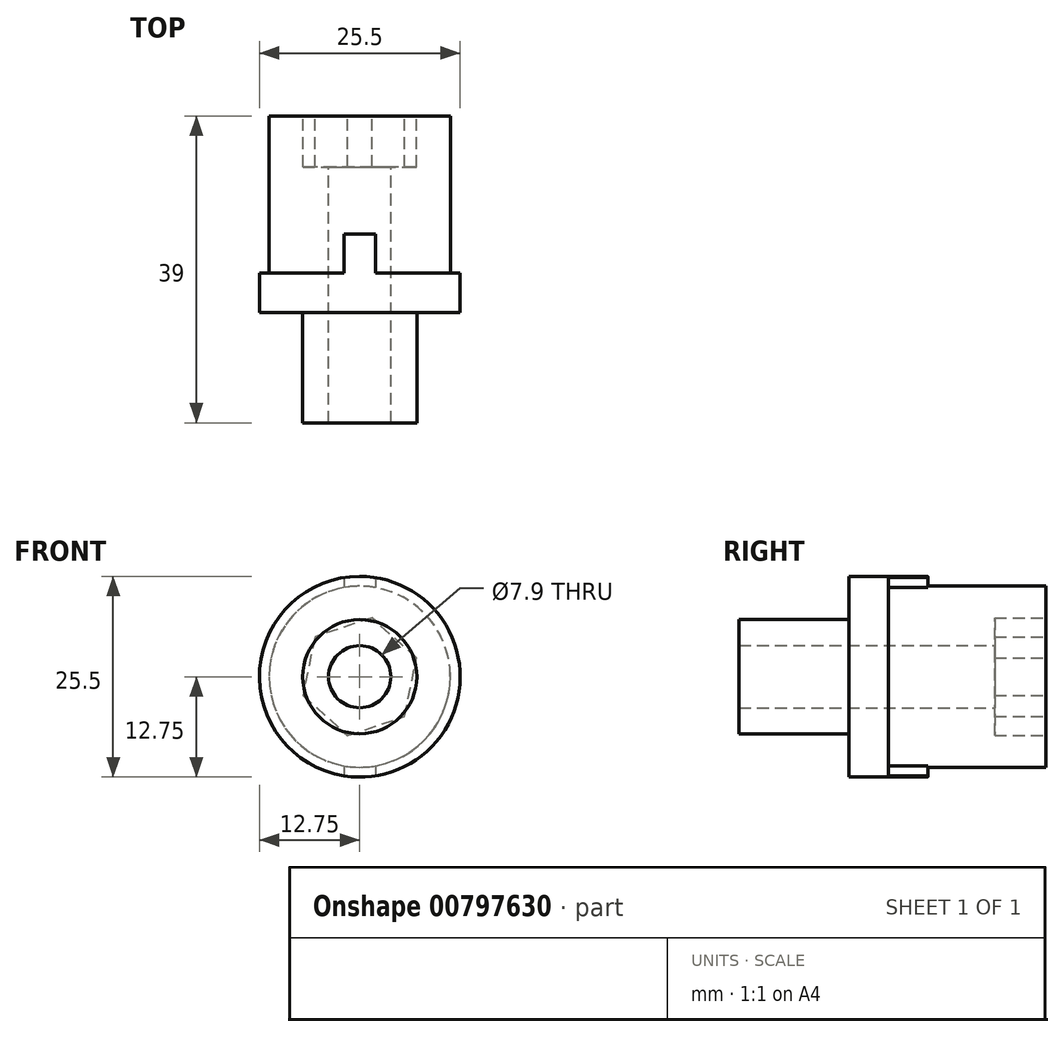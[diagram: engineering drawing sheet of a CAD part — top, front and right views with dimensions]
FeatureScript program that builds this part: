
annotation { "Feature Type Name" : "Feature", "Feature Type Description" : "" }
export const myFeature = defineFeature(function(context is Context, id is Id, definition is map)
    precondition{}
    {
        {
            var Q0;
            Q0=qCreatedBy(makeId("Front.planeOp"),FACE);
            var sketch = newSketch(context, id + "F0", { "sketchPlane" : qUnion([Q0])});
            skCircle(sketch, "E0", {"center": v(0, 0) * mm, "radius": 7.25 * mm});
            skSolve(sketch);
        }
        {
            var Q0;
            Q0=makeQuery(id+"F0.imprint","IMPRINT",FACE,{"disambiguationData":[TD([[makeQuery(id+"F0.imprint","IMPRINT",EDGE,{"derivedFrom":sQuery(id+"F0.wireOp",EDGE,"E0")}),1.0]])]});
            extrude(context, id + "F1", {"entities" : qUnion([Q0]), "depth" : 14 * mm, "offsetDistance" : 25 * mm});
        }
        {
            var Q0;
            Q0=makeQuery(id+"F1.opExtrude","CAP_FACE",FACE,{"disambiguationData":[OSD([sQuery(id+"F0.wireOp",EDGE,"E0")])],"isStart":true});
            var sketch = newSketch(context, id + "F2", { "sketchPlane" : qUnion([Q0])});
            skCircle(sketch, "E1", {"center": v(0, 0) * mm, "radius": 9.25 * mm});
            skCircle(sketch, "E2", {"center": v(0, 0) * mm, "radius": 11.25 * mm});
            skSolve(sketch);
        }
        {
            var Q0;
            Q0=makeQuery(id+"F1.opExtrude","CAP_FACE",FACE,{"disambiguationData":[OSD([sQuery(id+"F0.wireOp",EDGE,"E0")])],"isStart":false});
            var sketch = newSketch(context, id + "F3", { "sketchPlane" : qUnion([Q0])});
            skCircle(sketch, "E3", {"center": v(0, 0) * mm, "radius": 3 * mm});
            skSolve(sketch);
        }
        {
            var Q0;
            Q0=makeQuery(id+"F3.imprint","IMPRINT",FACE,{"disambiguationData":[TD([[makeQuery(id+"F3.imprint","IMPRINT",EDGE,{"derivedFrom":sQuery(id+"F3.wireOp",EDGE,"E3")}),1.0]])]});
            extrude(context, id + "F4", {"entities" : qUnion([Q0]), "operationType" : NewBodyOperationType.REMOVE, "endBound" : BoundingType.THROUGH_ALL, "oppositeDirection" : true, "depth" : 25 * mm, "offsetDistance" : 25 * mm});
        }
        {
            var Q0;
            Q0=makeQuery(id+"F2.imprint","IMPRINT",FACE,{"disambiguationData":[TD([[makeQuery(id+"F2.imprint","IMPRINT",EDGE,{"derivedFrom":sQuery(id+"F2.wireOp",EDGE,"E1")}),1.0]])]});
            cPlane(context, id + "F5", {"entities" : qUnion([Q0]), "cplaneType" : CPlaneType.OFFSET, "offset" : 0 * mm, "width" : 150 * mm, "height" : 150 * mm});
        }
        {
            var Q0;
            Q0=qCreatedBy(id+"F5.planeOp",FACE);
            var sketch = newSketch(context, id + "F6", { "sketchPlane" : qUnion([Q0])});
            skCircle(sketch, "E4", {"center": v(0, 0) * mm, "radius": 12.75 * mm});
            skSolve(sketch);
        }
        {
            var Q0;
            Q0=qSketchRegion(id+"F6",true);
            extrude(context, id + "F7", {"entities" : qUnion([Q0]), "operationType" : NewBodyOperationType.ADD, "depth" : 25 * mm, "offsetDistance" : 25 * mm});
        }
        {
            var Q0;
            Q0=makeQuery(id+"F7.opExtrude","CAP_FACE",FACE,{"disambiguationData":[OSD([sQuery(id+"F6.wireOp",EDGE,"E4")])],"isStart":false});
            var sketch = newSketch(context, id + "F8", { "sketchPlane" : qUnion([Q0])});
            skCircle(sketch, "E5", {"center": v(0, 0) * mm, "radius": 3.95 * mm});
            skSolve(sketch);
        }
        {
            var Q0;
            Q0=makeQuery(id+"F8.imprint","IMPRINT",FACE,{"disambiguationData":[TD([[makeQuery(id+"F8.imprint","IMPRINT",EDGE,{"derivedFrom":sQuery(id+"F8.wireOp",EDGE,"E5")}),1.0]])]});
            extrude(context, id + "F9", {"entities" : qUnion([Q0]), "operationType" : NewBodyOperationType.REMOVE, "endBound" : BoundingType.THROUGH_ALL, "oppositeDirection" : true, "depth" : 25 * mm, "offsetDistance" : 25 * mm});
        }
        {
            var Q0;
            Q0=makeQuery(id+"F7.opExtrude","CAP_FACE",FACE,{"disambiguationData":[OSD([sQuery(id+"F6.wireOp",EDGE,"E4")])],"isStart":false});
            var sketch = newSketch(context, id + "F10", { "sketchPlane" : qUnion([Q0])});
            skCircle(sketch, "E6", {"center": v(0, 0) * mm, "radius": 11.5 * mm});
            skSolve(sketch);
        }
        {
            var Q0;
            Q0=makeQuery(id+"F10.imprint","IMPRINT",FACE,{"disambiguationData":[TD([[makeQuery(id+"F10.imprint","IMPRINT",EDGE,{"derivedFrom":sQuery(id+"F10.wireOp",EDGE,"E6")}),-1.0]])]});
            extrude(context, id + "F11", {"entities" : qUnion([Q0]), "operationType" : NewBodyOperationType.REMOVE, "oppositeDirection" : true, "depth" : 20 * mm, "offsetDistance" : 25 * mm});
        }
        {
            var Q0;
            Q0=makeQuery(id+"F11.boolean.opBoolean","COPY",FACE,{"derivedFrom":makeQuery(id+"F11.opExtrude","CAP_FACE",FACE,{"disambiguationData":[OSD([sQuery(id+"F6.wireOp",EDGE,"E4"),sQuery(id+"F10.wireOp",EDGE,"E6")])],"isStart":false})});
            var sketch = newSketch(context, id + "F12", { "sketchPlane" : qUnion([Q0])});
            skLineSegment(sketch, "E7", {"start": v(0, 13.66) * mm, "end": v(0, -14.8) * mm, "construction": true});
            skLineSegment(sketch, "E8", {"start": v(-2, 12.6) * mm, "end": v(-2, 11.32) * mm});
            skLineSegment(sketch, "E9", {"start": v(2, 12.6) * mm, "end": v(2, 11.32) * mm});
            skLineSegment(sketch, "E10", {"start": v(-14.5, 0) * mm, "end": v(13.95, 0) * mm, "construction": true});
            skLineSegment(sketch, "E11.MirrorCS", {"start": v(-6, 12.6) * mm, "end": v(-6, 11.32) * mm});
            skLineSegment(sketch, "E12.MirrorCS", {"start": v(10.5, 0) * mm, "end": v(-17.95, 0) * mm, "construction": true});
            skLineSegment(sketch, "E13", {"start": v(-2, -11.32) * mm, "end": v(-2, -12.6) * mm});
            skLineSegment(sketch, "E14", {"start": v(2, -11.32) * mm, "end": v(2, -12.6) * mm});
            skPoint(sketch, "E15.MirrorCS.end.orphan", {"position": v(-6, 11.32) * mm});
            skPoint(sketch, "E15.MirrorCS.start.orphan", {"position": v(-6, 12.6) * mm});
            skSolve(sketch);
        }
        {
            var Q0;
            {var subQ0=sQuery(id+"F12.wireOp",EDGE,"E8");Q0=makeQuery(id+"F12.imprint","IMPRINT",FACE,{"disambiguationData":[TD([[makeQuery(id+"F12.imprint","IMPRINT",EDGE,{"derivedFrom":subQ0}),1.0]])]});}
            var Q1;
            {var subQ0=sQuery(id+"F12.wireOp",EDGE,"E13");Q1=makeQuery(id+"F12.imprint","IMPRINT",FACE,{"disambiguationData":[TD([[makeQuery(id+"F12.imprint","IMPRINT",EDGE,{"derivedFrom":subQ0}),1.0]])]});}
            extrude(context, id + "F13", {"entities" : qUnion([Q0, Q1]), "operationType" : NewBodyOperationType.ADD, "depth" : 5 * mm, "offsetDistance" : 25 * mm});
        }
        {
            var Q0;
            Q0=makeQuery(id+"F7.opExtrude","CAP_FACE",FACE,{"disambiguationData":[OSD([sQuery(id+"F6.wireOp",EDGE,"E4")])],"isStart":false});
            var sketch = newSketch(context, id + "F14", { "sketchPlane" : qUnion([Q0])});
            skCircle(sketch, "E16.cCircle", {"center": v(0, 0) * mm, "radius": 6.6 * mm, "construction": true});
            skLineSegment(sketch, "E16.0", {"start": v(-1.53, 7.46) * mm, "end": v(5.7, 5.06) * mm});
            skLineSegment(sketch, "E16.1", {"start": v(5.7, 5.06) * mm, "end": v(7.23, -2.4) * mm});
            skLineSegment(sketch, "E16.2", {"start": v(7.23, -2.4) * mm, "end": v(1.53, -7.46) * mm});
            skLineSegment(sketch, "E16.3", {"start": v(1.53, -7.46) * mm, "end": v(-5.7, -5.06) * mm});
            skLineSegment(sketch, "E16.4", {"start": v(-5.7, -5.06) * mm, "end": v(-7.23, 2.4) * mm});
            skLineSegment(sketch, "E16.5", {"start": v(-7.23, 2.4) * mm, "end": v(-1.53, 7.46) * mm});
            skPoint(sketch, "E16.0.midPoint", {"position": v(2.08, 6.26) * mm});
            skSolve(sketch);
        }
        {
            var Q0;
            Q0=makeQuery(id+"F14.imprint","IMPRINT",FACE,{"disambiguationData":[TD([[makeQuery(id+"F14.imprint","IMPRINT",EDGE,{"derivedFrom":sQuery(id+"F14.wireOp",EDGE,"E16.0")}),-1.0]])]});
            extrude(context, id + "F15", {"entities" : qUnion([Q0]), "operationType" : NewBodyOperationType.REMOVE, "oppositeDirection" : true, "depth" : 6.5 * mm, "offsetDistance" : 25 * mm});
        }
    });
